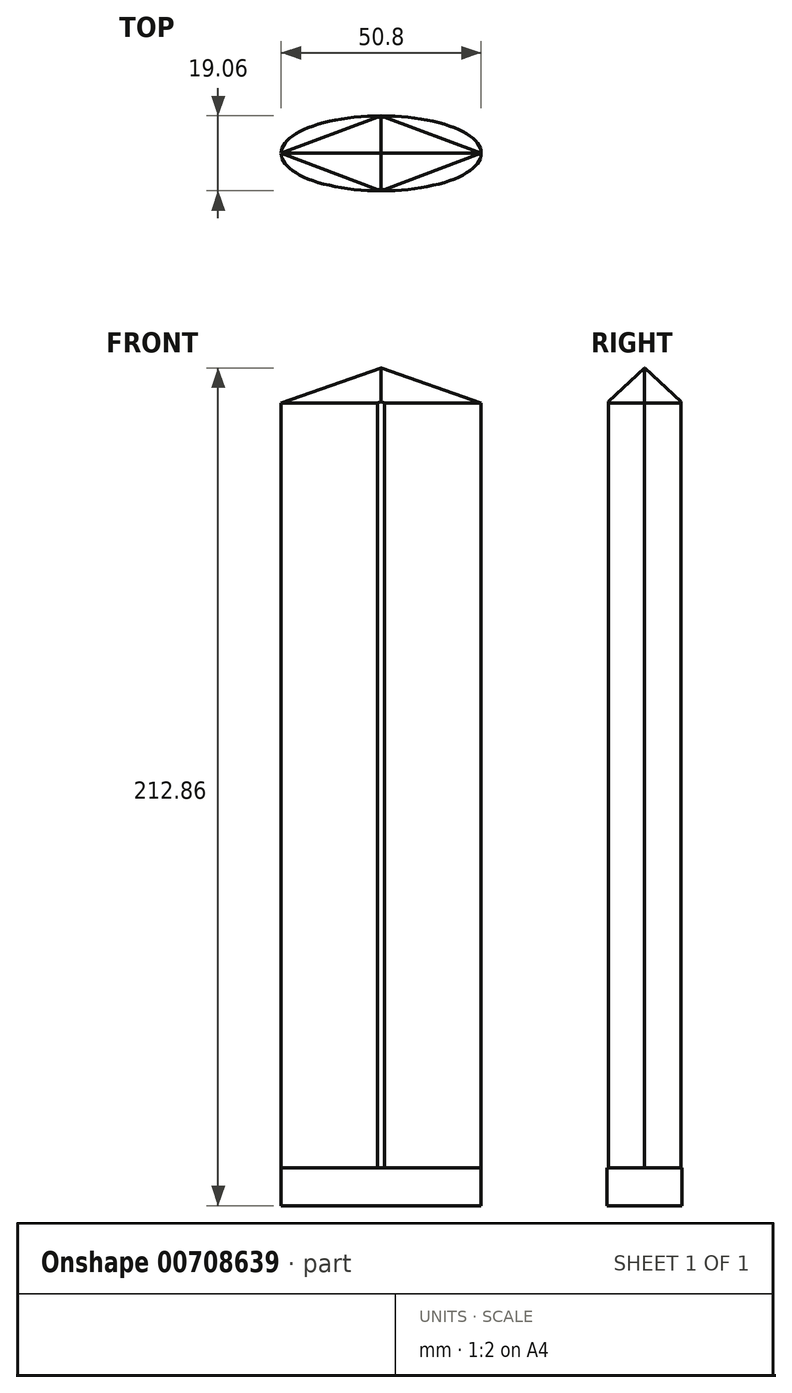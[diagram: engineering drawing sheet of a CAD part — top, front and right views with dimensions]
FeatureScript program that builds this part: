
annotation { "Feature Type Name" : "Feature", "Feature Type Description" : "" }
export const myFeature = defineFeature(function(context is Context, id is Id, definition is map)
    precondition{}
    {
        {
            var Q0;
            Q0=qCreatedBy(makeId("Top.planeOp"),FACE);
            var sketch = newSketch(context, id + "F0", { "sketchPlane" : qUnion([Q0])});
            skEllipse(sketch, "E0", {"center": v(0, 0) * mm, "majorRadius": 25.4 * mm, "minorRadius": 9.53 * mm, "majorAxis": v(-1, 0)});
            skSolve(sketch);
        }
        {
            var Q0;
            Q0 = qSketchRegion(id + "F0", true);
            extrude(context, id + "F1", {"entities" : qUnion([Q0]), "endBound" : BoundingType.SYMMETRIC, "oppositeDirection" : true, "depth" : 9.65 * mm, "offsetDistance" : 25.4 * mm});
        }
        {
            var Q0;
            Q0=makeQuery(id+"F1.opExtrude","CAP_FACE",FACE,{"disambiguationData":[OSD([sQuery(id+"F0.wireOp",EDGE,"E0")])],"isStart":true});
            var sketch = newSketch(context, id + "F2", { "sketchPlane" : qUnion([Q0])});
            skLineSegment(sketch, "E1", {"start": v(-25.4, 0) * mm, "end": v(0, 9.53) * mm});
            skLineSegment(sketch, "E2", {"start": v(0, 9.53) * mm, "end": v(25.4, 0) * mm});
            skLineSegment(sketch, "E3", {"start": v(25.4, 0) * mm, "end": v(0, -9.53) * mm});
            skLineSegment(sketch, "E4", {"start": v(0, -9.52) * mm, "end": v(-25.4, 0) * mm});
            skSolve(sketch);
        }
        {
            var Q0;
            Q0 = qSketchRegion(id + "F2", true);
            extrude(context, id + "F3", {"entities" : qUnion([Q0]), "operationType" : NewBodyOperationType.ADD, "depth" : 203.2 * mm, "offsetDistance" : 25.4 * mm});
        }
        {
            var Q0;
            Q0=makeQuery(id+"F3.opExtrude","CAP_FACE",FACE,{"disambiguationData":[OSD([sQuery(id+"F2.wireOp",EDGE,"E1"),sQuery(id+"F2.wireOp",EDGE,"E2"),sQuery(id+"F2.wireOp",EDGE,"E3"),sQuery(id+"F2.wireOp",EDGE,"E4")])],"isStart":false});
            chamfer(context, id + "F4", {"entities" : qUnion([Q0]), "width" : 8.9 * mm, "tangentPropagation" : true});
        }
        {
            var Q0;
            Q0=makeQuery(id+"F3.opExtrude","SWEPT_EDGE",EDGE,{"disambiguationData":[OSD([sQuery(id+"F0.wireOp",EDGE,"E0"),sQuery(id+"F2.wireOp",EDGE,"E3"),sQuery(id+"F2.wireOp",EDGE,"E4")])]});
            var Q1;
            Q1=makeQuery(id+"F3.opExtrude","SWEPT_EDGE",EDGE,{"disambiguationData":[OSD([sQuery(id+"F0.wireOp",EDGE,"E0"),sQuery(id+"F2.wireOp",EDGE,"E1"),sQuery(id+"F2.wireOp",EDGE,"E2")])]});
            chamfer(context, id + "F5", {"entities" : qUnion([Q0, Q1]), "width" : 2.54 * mm, "tangentPropagation" : true});
        }
    });
